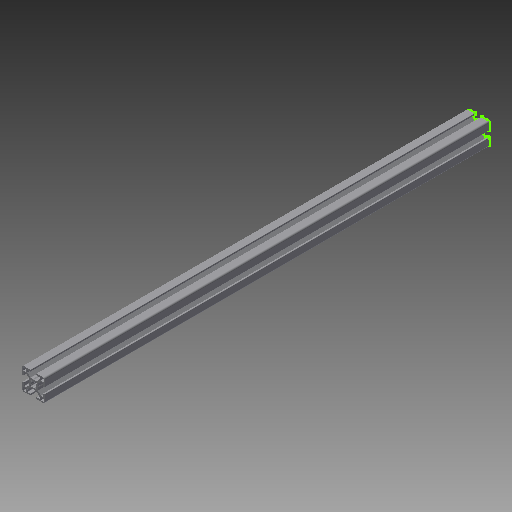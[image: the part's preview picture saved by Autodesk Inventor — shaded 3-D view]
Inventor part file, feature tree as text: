
AUTODESK INVENTOR PART (.ipt)
format: ipt  version: 2018 (Build 220112000, 112)  size: 355,328 bytes
history: native  units: mm
features: sketch x2, extrude x1, plane x1
ambient origin geometry x8: Origin, YZ Plane, XZ Plane, XY Plane, X Axis, Y Axis, Z Axis, Center Point
bodies: Solid1 (feature_tree)
feature tree (4):
  sketch  "Sketch1"  dims[d0=600.0mm d1=0.0mm]
  extrude  "Extrusion1"  [1 undecoded]
  plane  "Work Plane1"
  sketch  "Sketch3"
note: 1 required parameter value undecoded (feature->parameter linkage not recoverable at this tier; creation-order binding heuristic only, values carry confidence <= 0.55)
